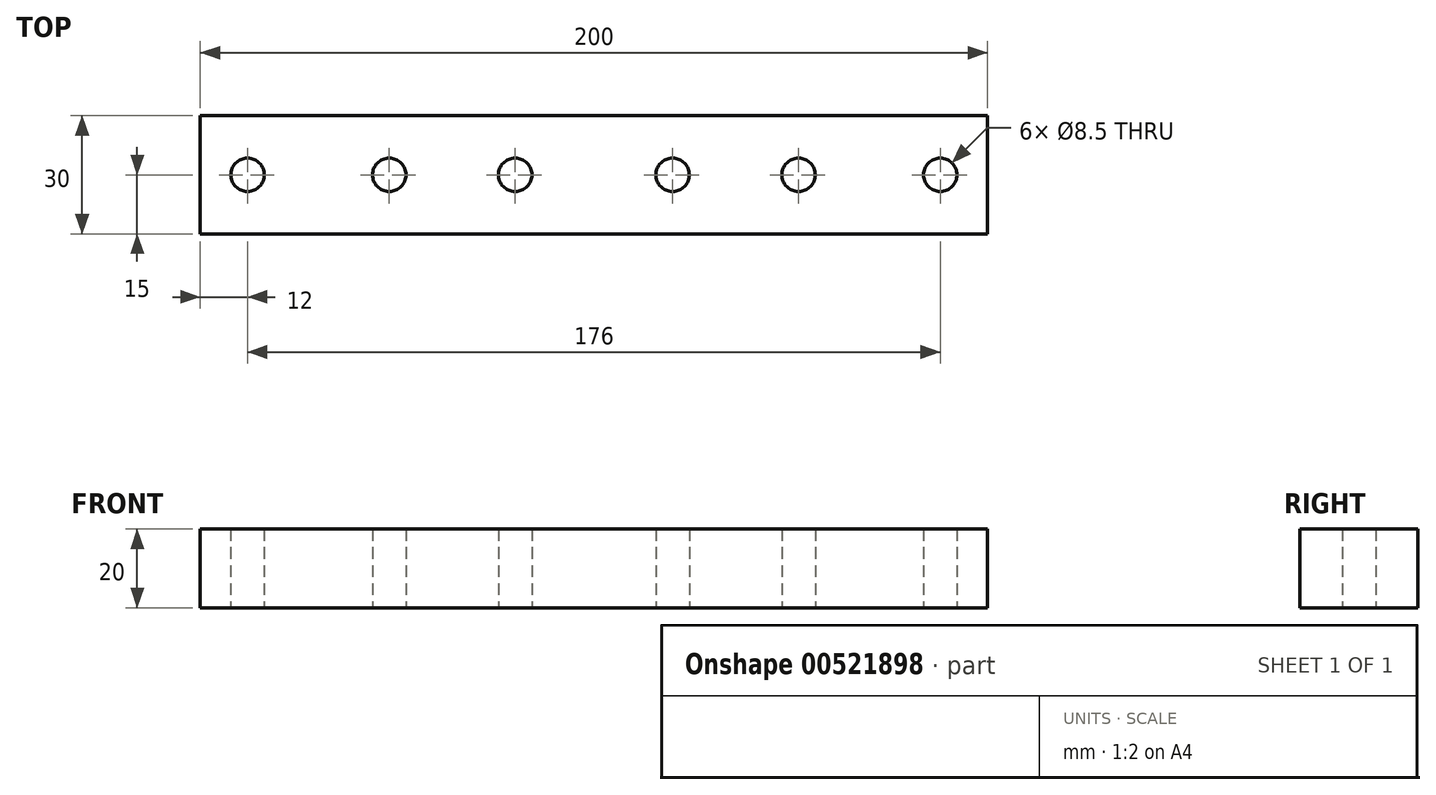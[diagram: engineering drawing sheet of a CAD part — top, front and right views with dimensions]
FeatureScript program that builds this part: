
annotation { "Feature Type Name" : "Feature", "Feature Type Description" : "" }
export const myFeature = defineFeature(function(context is Context, id is Id, definition is map)
    precondition{}
    {
        {
            var Q0;
            Q0=qCreatedBy(makeId("Top.planeOp"),FACE);
            var sketch = newSketch(context, id + "F0", { "sketchPlane" : qUnion([Q0])});
            skLineSegment(sketch, "E0.bottom", {"start": v(-100, 15) * mm, "end": v(100, 15) * mm});
            skLineSegment(sketch, "E0.top", {"start": v(-100, -15) * mm, "end": v(100, -15) * mm});
            skLineSegment(sketch, "E0.left", {"start": v(-100, 15) * mm, "end": v(-100, -15) * mm});
            skLineSegment(sketch, "E0.right", {"start": v(100, 15) * mm, "end": v(100, -15) * mm});
            skCircle(sketch, "E1", {"center": v(-88, 0) * mm, "radius": 4.25 * mm});
            skPoint(sketch, "E1.centerSnap0", {"position": v(-100, 0) * mm});
            skCircle(sketch, "E2", {"center": v(-52, 0) * mm, "radius": 4.25 * mm});
            skCircle(sketch, "E3", {"center": v(52, 0) * mm, "radius": 4.25 * mm});
            skCircle(sketch, "E4", {"center": v(88, 0) * mm, "radius": 4.25 * mm});
            skCircle(sketch, "E5", {"center": v(-20, 0) * mm, "radius": 4.25 * mm});
            skCircle(sketch, "E6", {"center": v(20, 0) * mm, "radius": 4.25 * mm});
            skSolve(sketch);
        }
        {
            var Q0;
            Q0 = qSketchRegion(id + "F0", true);
            extrude(context, id + "F1", {"entities" : qUnion([Q0]), "depth" : 20 * mm, "offsetDistance" : 25 * mm});
        }
    });
